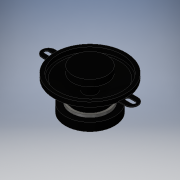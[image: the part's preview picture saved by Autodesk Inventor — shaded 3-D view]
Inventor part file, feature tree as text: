
AUTODESK INVENTOR PART (.ipt)
format: ipt  version: 2016 (Build 200138000, 138)  size: 218,112 bytes
history: native  units: mm
features: sketch x4, projected_geometry x3, extrude x2, revolve x2, mirror x1
ambient origin geometry x8: Origin, YZ Plane, XZ Plane, XY Plane, X Axis, Y Axis, Z Axis, Center Point
bodies: Solid1 (feature_tree)
feature tree (12):
  extrude  "Extrusion1"  Depth=78.0mm
  revolve  "Revolution1"  [1 undecoded]
  revolve  "Revolution2"  [1 undecoded]
  extrude  "Extrusion2"  Depth=3.0mm
  mirror  "Mirror1"
  sketch  "Sketch1"  dims[d0=87.0mm d1=78.0mm]
  sketch  "Sketch2"  dims[d2=5.5mm d3=0.0mm d4=38.5mm]
  projected_geometry  "Projected Loop1"
  sketch  "Sketch3"  dims[d5=30.0mm d6=16.0mm]
  projected_geometry  "Projected Loop2"
  sketch  "Sketch4"  dims[d7=7.0mm d8=3.0mm d9=7.0mm d10=3.0mm d11=3.0mm d12=90.0deg d13=8.0mm d14=31.0mm d15=21.0mm d16=8.0mm d17=90.0deg d18=104.0mm d19=3.5mm d20=4.87mm d21=8.0mm d22=8.0mm d23=1.0mm d24=0.0mm]
  projected_geometry  "Projected Loop3"
note: 2 required parameter values undecoded (feature->parameter linkage not recoverable at this tier; creation-order binding heuristic only, values carry confidence <= 0.55)
